# Revit family: BC_COMATEC_Alimentation-régulée-AL12-2DIN_LOD200
name_source: partatom
category: Installations électriques
revit_build: Autodesk Revit 2017 (Build: 20181011_1645(x64)
units: mm (PartAtom-declared; Revit-internal decimal feet)

## family parameters
Basée sur le plan de construction = Non
Conserver l'orientation des annotations = Non
Cote de connecteur circulaire = Utiliser le diamètre
Couper avec des vides une fois chargée = Non
Numéro OmniClass = 23.80.00.00
Partagée = Non
Point de calcul de pièce = Non
Titre OmniClass = Electric Power and Lighting
Toujours verticalement = Oui
Type d'élément = Normal

## types (1)
- Alimentation régulée AL12/2DIN
    Altitude de Fonctionnement = 2000000 mm  [stored 6561.68 ft]
    Classe d'isolation électrique = Classe II
    Code Produit = AL122DINRD
    Commentaires du type = Rail-Din pour tableaux domotique
    Compatibilité électromagnétique - EN61000-3-2(3) = conforme
    Consommation = 2 W
    Correction du facteur de puissance = Non
    Courant d'Appel = 20 A
    Courant d'absorption max en entrée = 1 A
    Courant nominal en sortie = 2 A
    Courant à vide en entrée = 0.2
    Cycle d'utilisation = Permanent
    Description = Alimentation éléctrique
    Directives ErP - Dir. 2011/65/EU Dir. 2015/863 EN50581 = conforme
    Directives RoHS - Dir. 2009/125/ECDir. 2011/65/EU Dir. 2015/863 EN50581 = conforme
    Durée de Vie = 100000.0 h
    Emissions électromagnétiques - EN55032/B  = conforme
    Fabricant = COMATEC
    Fréquence maximale d'entrée = 63 Hz
    Fréquence minimale d'entrée  = 47 Hz
    Hauteur Hors Tout = 70 mm  [stored 0.229659 ft]
    Largeur Hors Tout = 53 mm  [stored 0.173885 ft]
    Marque de Certification = CE
    Modèle = Alimentation régulée AL12/2DIN
    Nombre de modules = 3
    Norme de Sécurité = EN62368
    Ondulation max de sortie = 90
    Plage d'Humidité de Fonctionnement = 0 à 90 %
    Profondeur Hors Tout = 95 mm
    Puissance de sortie  = 24 W
    Refroidissement = Statique
    Rendement = 0.83
    Sensibilité électromagnétique - EN55024 = conforme
    Signalement LED  = Oui
    Temps d'installation = 0.1 h
    Tension AC Min = 100 V
    Tension AC max = 240 V
    Tension de sortie maximum  = SELV
    Tension nominale de sortie = 12 V
    Type d'Alimentation = à découpage type Flyback
    Type de Charge = Générique
    Type de protection = Surcharge d'entrée. Surcharge de sortie. Surtension de sortie. Court-circuits. Surtempérature
    Valeur Basse de la Plage de Température = -10 °C
    Valeur Haute de la Plage de Tempérarure = 45 °C

note: [stored X ft] marks values corroborated as IEEE doubles in the binary element streams (Revit-internal decimal feet)
